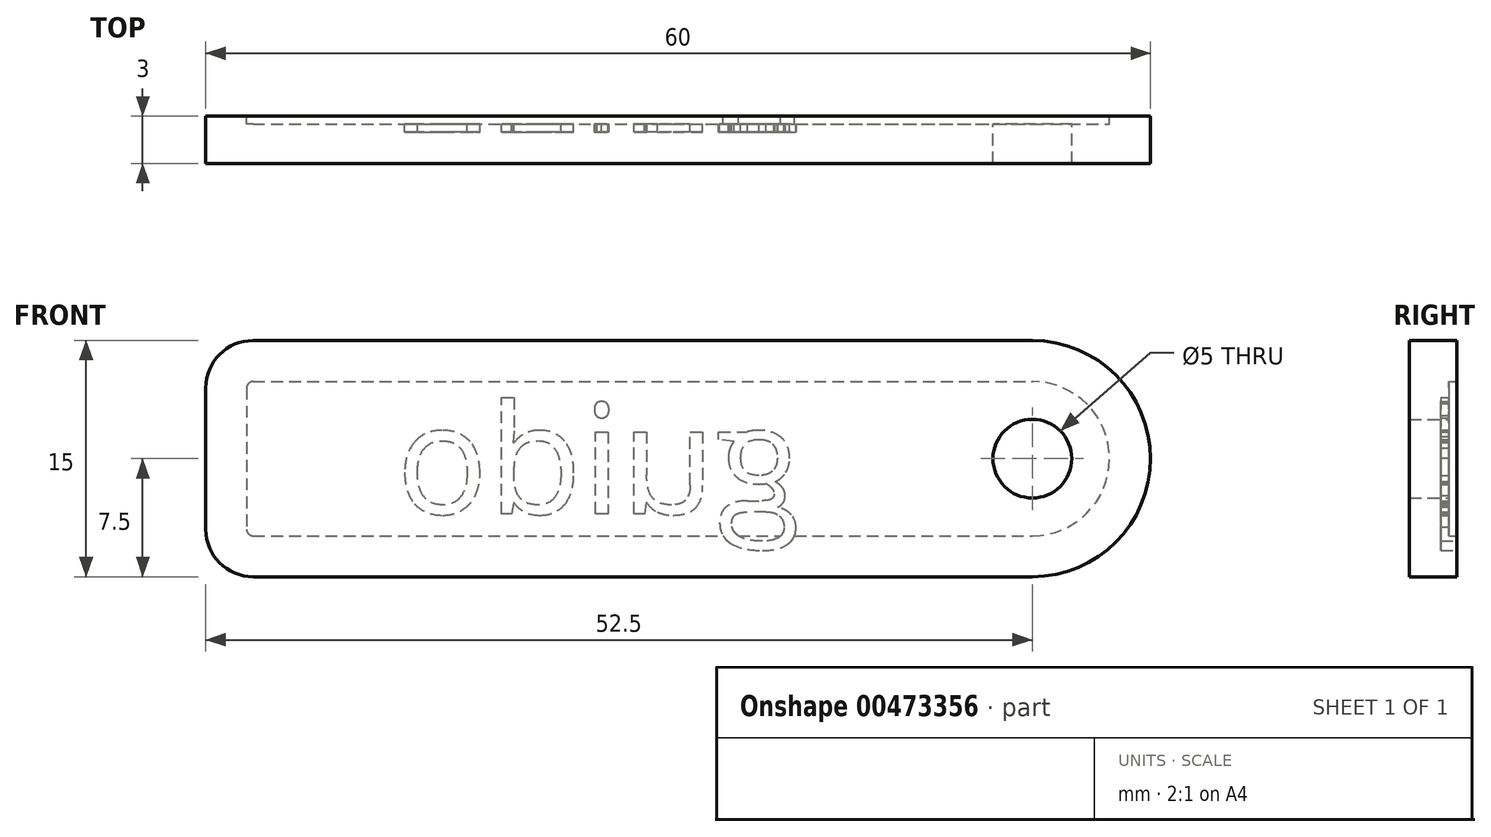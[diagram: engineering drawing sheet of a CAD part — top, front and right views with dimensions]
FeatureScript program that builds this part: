
annotation { "Feature Type Name" : "Feature", "Feature Type Description" : "" }
export const myFeature = defineFeature(function(context is Context, id is Id, definition is map)
    precondition{}
    {
        {
            var Q0;
            Q0=qCreatedBy(makeId("Front.planeOp"),FACE);
            var sketch = newSketch(context, id + "F0", { "sketchPlane" : qUnion([Q0])});
            skLineSegment(sketch, "E0.bottom", {"start": v(3, 7.5) * mm, "end": v(52.5, 7.5) * mm});
            skLineSegment(sketch, "E0.top", {"start": v(3, -7.5) * mm, "end": v(52.5, -7.5) * mm});
            skLineSegment(sketch, "E0.left", {"start": v(0, 4.5) * mm, "end": v(0, -4.5) * mm});
            skCircle(sketch, "E1", {"center": v(52.5, 0) * mm, "radius": 2.5 * mm});
            skArc(sketch, "E2", {"start": v(52.5, -7.5) * mm, "mid": v(60, 0) * mm, "end": v(52.5, 7.5) * mm});
            skPoint(sketch, "E3.visualSharp", {"position": v(0, -7.5) * mm});
            skArc(sketch, "E3.filletArc", {"start": v(0, -4.5) * mm, "mid": v(0.88, -6.62) * mm, "end": v(3, -7.5) * mm});
            skPoint(sketch, "E4.visualSharp", {"position": v(0, 7.5) * mm});
            skArc(sketch, "E4.filletArc", {"start": v(3, 7.5) * mm, "mid": v(0.88, 6.62) * mm, "end": v(0, 4.5) * mm});
            skSolve(sketch);
        }
        {
            var Q0;
            Q0=makeQuery(id+"F0.imprint","IMPRINT",FACE,{"disambiguationData":[TD([[makeQuery(id+"F0.imprint","IMPRINT",EDGE,{"derivedFrom":sQuery(id+"F0.wireOp",EDGE,"He5UYaIb-PRW4-bSrv-m294-Xdddkvdjzh15")}),-1.0]])]});
            var Q1;
            Q1=makeQuery(id+"F0.imprint","IMPRINT",FACE,{"disambiguationData":[TD([[makeQuery(id+"F0.imprint","IMPRINT",EDGE,{"derivedFrom":sQuery(id+"F0.wireOp",EDGE,"E0.right")}),1.0]])]});
            var Q2;
            Q2=makeQuery(id+"F0.imprint","IMPRINT",FACE,{"disambiguationData":[TD([[makeQuery(id+"F0.imprint","IMPRINT",EDGE,{"derivedFrom":sQuery(id+"F0.wireOp",EDGE,"E0.bottom")}),-1.0]])]});
            extrude(context, id + "F1", {"entities" : qUnion([Q0, Q1, Q2]), "depth" : 3 * mm});
        }
        {
            var Q0;
            Q0=makeQuery(id+"F1.opExtrude","CAP_FACE",FACE,{"disambiguationData":[OSD([sQuery(id+"F0.wireOp",EDGE,"E0.bottom"),sQuery(id+"F0.wireOp",EDGE,"E0.top"),sQuery(id+"F0.wireOp",EDGE,"E0.left"),sQuery(id+"F0.wireOp",EDGE,"E1"),sQuery(id+"F0.wireOp",EDGE,"E2"),sQuery(id+"F0.wireOp",EDGE,"E3.filletArc"),sQuery(id+"F0.wireOp",EDGE,"E4.filletArc")])],"isStart":true});
            var sketch = newSketch(context, id + "F2", { "sketchPlane" : qUnion([Q0])});
            skText(sketch, "E5", { "text": "guido\n", "fontName": "OpenSans-Regular.ttf"});
            const initialGuessF2  = {"E5": [-0.03767, -0.0035, 1, 0, 0.007]};
            skSetInitialGuess(sketch, initialGuessF2);
            skSolve(sketch);
        }
        {
            var Q0;
            Q0 = qSketchRegion(id + "F2", true);
            extrude(context, id + "F3", {"entities" : qUnion([Q0]), "operationType" : NewBodyOperationType.REMOVE, "oppositeDirection" : true, "depth" : 1 * mm});
        }
        {
            var Q0;
            {var subQ0=sQuery(id+"F0.wireOp",EDGE,"E0.left");var subQ1=sQuery(id+"F0.wireOp",EDGE,"E4.filletArc");var subQ2=sQuery(id+"F0.wireOp",EDGE,"E3.filletArc");var subQ3=sQuery(id+"F0.wireOp",EDGE,"E2");var subQ4=sQuery(id+"F0.wireOp",EDGE,"E0.bottom");var subQ5=sQuery(id+"F0.wireOp",EDGE,"E1");var subQ6=sQuery(id+"F0.wireOp",EDGE,"E0.top");Q0=makeQuery(id+"F3.boolean.opBoolean","SPLIT",FACE,{"disambiguationData":[TD([makeQuery(id+"F1.opExtrude","SWEPT_FACE",FACE,{"disambiguationData":[OSD([subQ4])]})])],"derivedFrom":makeQuery(id+"F1.opExtrude","CAP_FACE",FACE,{"disambiguationData":[OSD([subQ4,subQ6,subQ0,subQ5,subQ3,subQ2,subQ1])],"isStart":true})});}
            var sketch = newSketch(context, id + "F4", { "sketchPlane" : qUnion([Q0])});
            skLineSegment(sketch, "E6.0", {"start": v(-3, 2.5) * mm, "end": v(-52.5, 2.5) * mm});
            skArc(sketch, "E6.1", {"start": v(-52.5, -2.5) * mm, "mid": v(-55, 0) * mm, "end": v(-52.5, 2.5) * mm});
            skArc(sketch, "E7.0", {"start": v(-3, 4.9) * mm, "mid": v(-2.72, 4.78) * mm, "end": v(-2.6, 4.5) * mm});
            skArc(sketch, "E7.1", {"start": v(-52.5, -4.9) * mm, "mid": v(-57.4, 0) * mm, "end": v(-52.5, 4.9) * mm});
            skLineSegment(sketch, "E7.2", {"start": v(-3, -4.9) * mm, "end": v(-52.5, -4.9) * mm});
            skLineSegment(sketch, "E7.3", {"start": v(-3, 4.9) * mm, "end": v(-52.5, 4.9) * mm});
            skArc(sketch, "E7.4", {"start": v(-2.6, -4.5) * mm, "mid": v(-2.72, -4.78) * mm, "end": v(-3, -4.9) * mm});
            skLineSegment(sketch, "E7.5", {"start": v(-2.6, 4.5) * mm, "end": v(-2.6, -4.5) * mm});
            skSolve(sketch);
        }
        {
            var Q0;
            Q0 = qSketchRegion(id + "F4", true);
            extrude(context, id + "F5", {"entities" : qUnion([Q0]), "operationType" : NewBodyOperationType.REMOVE, "oppositeDirection" : true, "depth" : 0.5 * mm});
        }
    });
